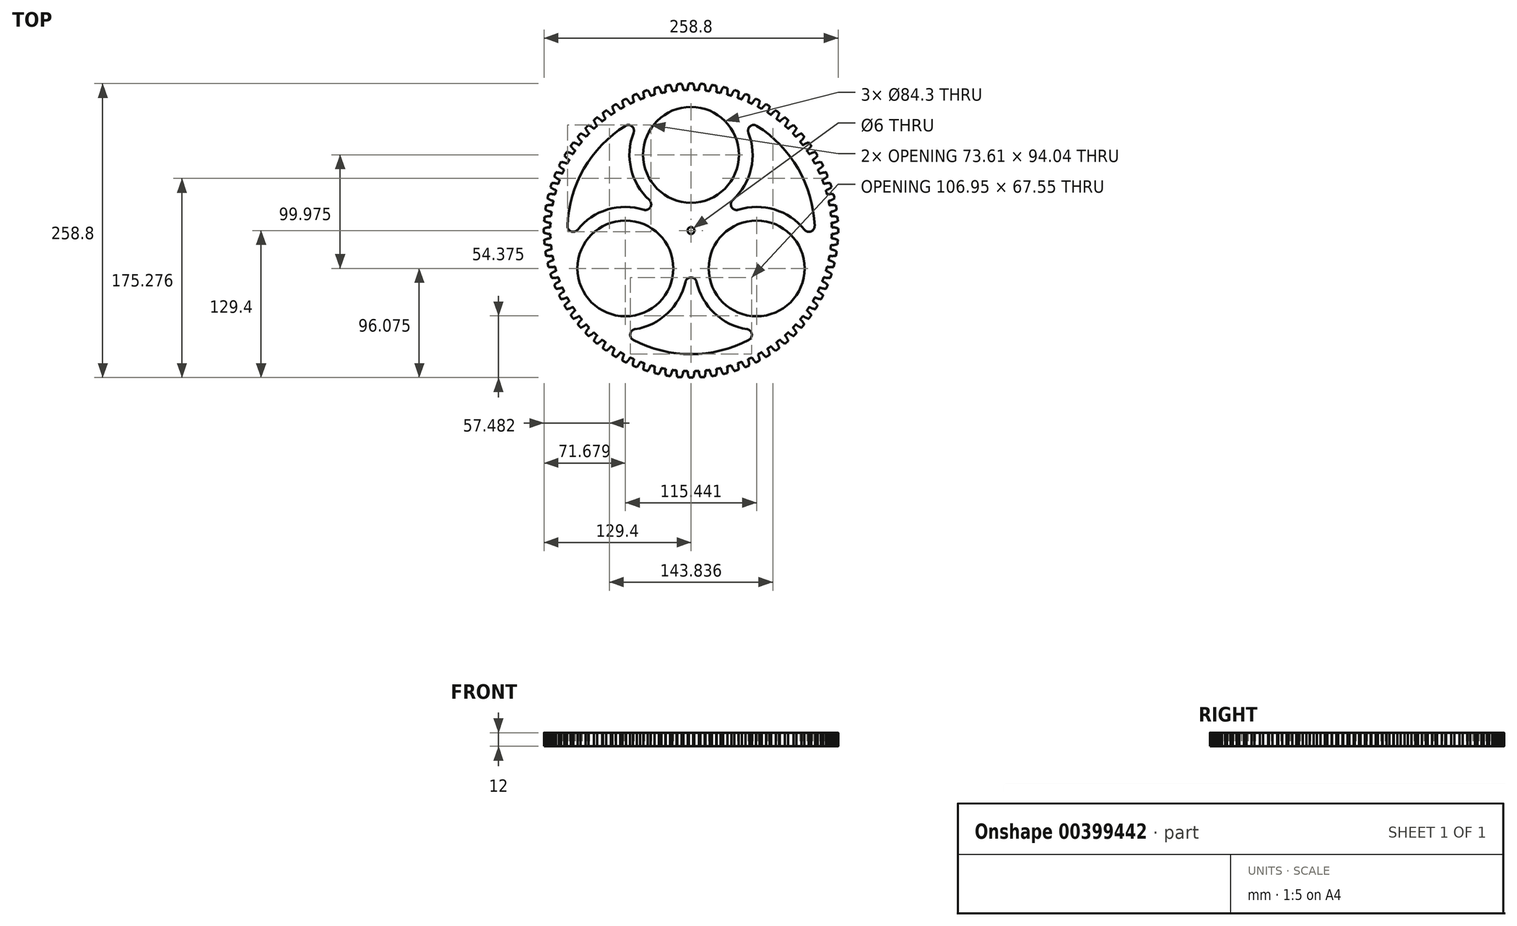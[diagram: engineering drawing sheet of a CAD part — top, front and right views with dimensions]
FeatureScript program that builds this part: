
annotation { "Feature Type Name" : "Feature", "Feature Type Description" : "" }
export const myFeature = defineFeature(function(context is Context, id is Id, definition is map)
    precondition{}
    {
        {
            var Q0;
            Q0=qCreatedBy(makeId("Top.planeOp"),FACE);
            var sketch = newSketch(context, id + "F0", { "sketchPlane" : qUnion([Q0])});
            skCircle(sketch, "E0", {"center": v(0, 0) * mm, "radius": 127 * mm, "construction": true});
            skCircle(sketch, "E1", {"center": v(0, 0) * mm, "radius": 115 * mm, "construction": true});
            skCircle(sketch, "E2", {"center": v(0, 0) * mm, "radius": 123.8 * mm, "construction": true});
            skCircle(sketch, "E3", {"center": v(0, 0) * mm, "radius": 129.4 * mm, "construction": true});
            skLineSegment(sketch, "E4", {"start": v(0, 0) * mm, "end": v(2.5, 126.98) * mm, "construction": true});
            skFitSpline(sketch, "E5", {"points": [v(1.9, 129.39) * mm, v(2.91, 123.77) * mm], "startDerivative": vector(2.37, -8.21) * mm, "endDerivative": vector(0.04, -2.85) * mm});
            skLineSegment(sketch, "E6", {"start": v(-34.3, 118.96) * mm, "end": v(1.9, 129.39) * mm, "construction": true});
            skLineSegment(sketch, "E7", {"start": v(1.86, 129.48) * mm, "end": v(1.92, 129.3) * mm, "construction": true});
            skLineSegment(sketch, "E8", {"start": v(2.47, 127.07) * mm, "end": v(2.51, 126.88) * mm, "construction": true});
            skLineSegment(sketch, "E9", {"start": v(2.7, 125.87) * mm, "end": v(2.73, 125.67) * mm, "construction": true});
            skLineSegment(sketch, "E10", {"start": v(-25.24, 121.2) * mm, "end": v(2.5, 126.98) * mm, "construction": true});
            skLineSegment(sketch, "E11", {"start": v(-19.35, 122.28) * mm, "end": v(2.72, 125.77) * mm, "construction": true});
            skLineSegment(sketch, "E12", {"start": v(-30.97, 119.86) * mm, "end": v(2.16, 128.42) * mm, "construction": true});
            skLineSegment(sketch, "E13", {"start": v(2.13, 128.52) * mm, "end": v(2.18, 128.32) * mm, "construction": true});
            skLineSegment(sketch, "E14", {"start": v(-27.24, 120.77) * mm, "end": v(2.4, 127.45) * mm, "construction": true});
            skLineSegment(sketch, "E15", {"start": v(2.37, 127.55) * mm, "end": v(2.41, 127.35) * mm, "construction": true});
            skLineSegment(sketch, "E16", {"start": v(-12.86, 123.13) * mm, "end": v(2.85, 124.77) * mm, "construction": true});
            skLineSegment(sketch, "E17", {"start": v(2.84, 124.87) * mm, "end": v(2.86, 124.67) * mm, "construction": true});
            skArc(sketch, "E18", {"start": v(1.9, 129.39) * mm, "mid": v(0.95, 129.4) * mm, "end": v(0, 129.4) * mm});
            skSolve(sketch);
        }
        {
            var Q0;
            Q0=qCreatedBy(makeId("Top.planeOp"),FACE);
            var sketch = newSketch(context, id + "F1", { "sketchPlane" : qUnion([Q0])});
            skArc(sketch, "E19.0", {"start": v(-2.91, 123.77) * mm, "mid": v(0, -123.8) * mm, "end": v(2.91, 123.77) * mm});
            skCircle(sketch, "E20", {"center": v(0, 0) * mm, "radius": 3 * mm});
            skArc(sketch, "E21.0", {"start": v(1.9, 129.39) * mm, "mid": v(0.95, 129.4) * mm, "end": v(0, 129.4) * mm});
            skFitSpline(sketch, "E22.0", {"points": [v(1.9, 129.39) * mm, v(2.68, 126.65) * mm, v(2.9, 124.72) * mm, v(2.91, 123.77) * mm]});
            skArc(sketch, "E23.MirrorCS", {"start": v(-1.9, 129.39) * mm, "mid": v(-0.95, 129.4) * mm, "end": v(0, 129.4) * mm});
            skFitSpline(sketch, "E24.MirrorCS", {"points": [v(-1.9, 129.39) * mm, v(-2.68, 126.65) * mm, v(-2.9, 124.72) * mm, v(-2.91, 123.77) * mm]});
            skSolve(sketch);
        }
        {
            var Q0;
            Q0=qSketchRegion(id+"F1",true);
            extrude(context, id + "F2", {"entities" : qUnion([Q0]), "depth" : 12 * mm});
        }
        {
            var Q0;
            Q0=makeQuery(id+"F2.opExtrude","SWEPT_BODY",BODY,{"disambiguationData":[OSD([sQuery(id+"F1.wireOp",EDGE,"eeb95daa-9a2c-4d3b-b40b-bc04c77fced4.1"),sQuery(id+"F1.wireOp",EDGE,"89ce5ca7-42de-484d-9174-436fac9ca7f20.MirrorCS"),sQuery(id+"F1.wireOp",EDGE,"E19.0"),sQuery(id+"F1.wireOp",EDGE,"E20"),sQuery(id+"F1.wireOp",EDGE,"5248a19e-9ef0-46ba-9073-8b5a409f4121.0"),sQuery(id+"F1.wireOp",EDGE,"a3f9b43a-bdc4-48c8-ab19-a17a6acebfe10.MirrorCS")])]});
            var Q1;
            Q1=makeQuery(id+"F2.opExtrude","SWEPT_FACE",FACE,{"disambiguationData":[OSD([sQuery(id+"F1.wireOp",EDGE,"E20")])]});
            circularPattern(context, id + "F3", {"operationType" : NewBodyOperationType.ADD, "entities" : qUnion([Q0]), "axis" : qUnion([Q1]), "angle" : 360 * degree, "instanceCount" : 80, "equalSpace" : true});
        }
        {
            var Q0;
            Q0=qCreatedBy(makeId("Top.planeOp"),FACE);
            var sketch = newSketch(context, id + "F4", { "sketchPlane" : qUnion([Q0])});
            skArc(sketch, "E25", {"start": v(-50.87, -96.18) * mm, "mid": v(0, -108.8) * mm, "end": v(50.87, -96.18) * mm});
            skCircle(sketch, "E26", {"center": v(0, 0) * mm, "radius": 12.5 * mm, "construction": true});
            skCircle(sketch, "E27", {"center": v(0, 66.65) * mm, "radius": 42.15 * mm});
            skCircle(sketch, "E28", {"center": v(57.72, -33.33) * mm, "radius": 42.15 * mm});
            skCircle(sketch, "E29", {"center": v(-57.72, -33.32) * mm, "radius": 42.15 * mm});
            skArc(sketch, "E30", {"start": v(-49.3, -86.82) * mm, "mid": v(-20.68, -72.83) * mm, "end": v(-4.88, -45.16) * mm});
            skArc(sketch, "E31", {"start": v(-50.53, 86.1) * mm, "mid": v(-52.73, 54.32) * mm, "end": v(-36.67, 26.8) * mm});
            skArc(sketch, "E32", {"start": v(99.84, 0.7) * mm, "mid": v(73.4, 18.5) * mm, "end": v(41.55, 18.35) * mm});
            skLineSegment(sketch, "E33", {"start": v(0, 66.65) * mm, "end": v(-57.72, -33.33) * mm, "construction": true});
            skLineSegment(sketch, "E34", {"start": v(57.72, -33.33) * mm, "end": v(0, 66.65) * mm, "construction": true});
            skLineSegment(sketch, "E35", {"start": v(-57.72, -33.32) * mm, "end": v(57.72, -33.33) * mm, "construction": true});
            skArc(sketch, "E36.trimOffspring", {"start": v(108.73, 4.04) * mm, "mid": v(94.22, 54.4) * mm, "end": v(57.86, 92.14) * mm});
            skArc(sketch, "E37.trimOffspring", {"start": v(-57.86, 92.14) * mm, "mid": v(-94.22, 54.4) * mm, "end": v(-108.73, 4.04) * mm});
            skPoint(sketch, "E38.visualSharp", {"position": v(-42.56, 100.13) * mm});
            skArc(sketch, "E38.filletArc", {"start": v(-50.53, 86.1) * mm, "mid": v(-52.02, 91.77) * mm, "end": v(-57.86, 92.14) * mm});
            skPoint(sketch, "E39.visualSharp", {"position": v(-108, -13.2) * mm});
            skArc(sketch, "E39.filletArc", {"start": v(-108.73, 4.04) * mm, "mid": v(-105.48, -0.83) * mm, "end": v(-99.84, 0.7) * mm});
            skPoint(sketch, "E40.visualSharp", {"position": v(-65.44, -86.92) * mm});
            skArc(sketch, "E40.filletArc", {"start": v(-49.3, -86.82) * mm, "mid": v(-53.46, -90.93) * mm, "end": v(-50.87, -96.18) * mm});
            skPoint(sketch, "E41.visualSharp", {"position": v(65.44, -86.92) * mm});
            skArc(sketch, "E41.filletArc", {"start": v(50.87, -96.18) * mm, "mid": v(53.46, -90.93) * mm, "end": v(49.3, -86.82) * mm});
            skPoint(sketch, "E42.visualSharp", {"position": v(108, -13.2) * mm});
            skArc(sketch, "E42.filletArc", {"start": v(99.84, 0.7) * mm, "mid": v(105.48, -0.83) * mm, "end": v(108.73, 4.04) * mm});
            skPoint(sketch, "E43.visualSharp", {"position": v(42.56, 100.13) * mm});
            skArc(sketch, "E43.filletArc", {"start": v(57.86, 92.14) * mm, "mid": v(52.02, 91.77) * mm, "end": v(50.53, 86.1) * mm});
            skArc(sketch, "E44.trimOffspring", {"start": v(36.67, 26.8) * mm, "mid": v(52.73, 54.32) * mm, "end": v(50.53, 86.1) * mm});
            skArc(sketch, "E45.trimOffspring", {"start": v(4.88, -45.16) * mm, "mid": v(20.68, -72.83) * mm, "end": v(49.3, -86.82) * mm});
            skArc(sketch, "E46.trimOffspring", {"start": v(-41.55, 18.35) * mm, "mid": v(-73.4, 18.5) * mm, "end": v(-99.84, 0.7) * mm});
            skArc(sketch, "E47.filletArc", {"start": v(36.67, 26.8) * mm, "mid": v(35.72, 20.62) * mm, "end": v(41.55, 18.35) * mm});
            skArc(sketch, "E48.filletArc", {"start": v(-41.55, 18.35) * mm, "mid": v(-35.72, 20.63) * mm, "end": v(-36.67, 26.8) * mm});
            skArc(sketch, "E49.filletArc", {"start": v(4.88, -45.16) * mm, "mid": v(0, -41.25) * mm, "end": v(-4.88, -45.16) * mm});
            skSolve(sketch);
        }
        {
            var Q0;
            Q0=qSketchRegion(id+"F4",true);
            extrude(context, id + "F5", {"entities" : qUnion([Q0]), "operationType" : NewBodyOperationType.REMOVE, "endBound" : BoundingType.THROUGH_ALL, "depth" : 25 * mm});
        }
    });
